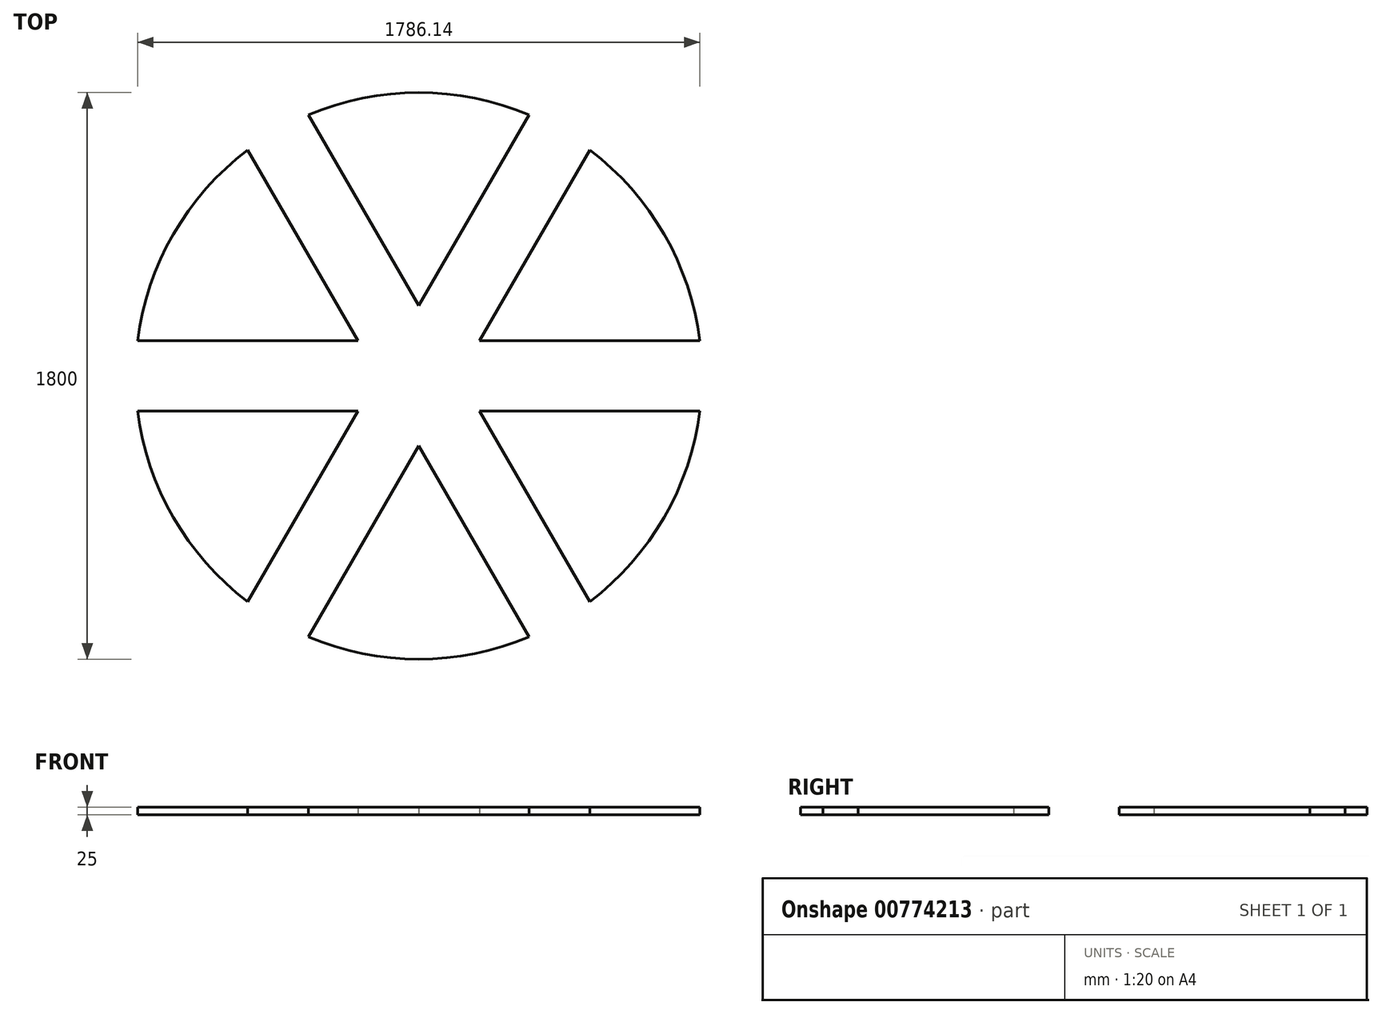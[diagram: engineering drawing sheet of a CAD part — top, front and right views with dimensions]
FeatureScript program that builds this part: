
annotation { "Feature Type Name" : "Feature", "Feature Type Description" : "" }
export const myFeature = defineFeature(function(context is Context, id is Id, definition is map)
    precondition{}
    {
        {
            var Q0;
            Q0=qCreatedBy(makeId("Top.planeOp"),FACE);
            var sketch = newSketch(context, id + "F0", { "sketchPlane" : qUnion([Q0])});
            skCircle(sketch, "E0", {"center": v(0, 0) * mm, "radius": 700 * mm});
            skCircle(sketch, "E1", {"center": v(0, 0) * mm, "radius": 900 * mm});
            skLineSegment(sketch, "E2", {"start": v(-350, 606.22) * mm, "end": v(-350, 829.16) * mm, "construction": true});
            skLineSegment(sketch, "E3", {"start": v(350, 606.22) * mm, "end": v(350, 829.16) * mm, "construction": true});
            skLineSegment(sketch, "E4", {"start": v(-350, 829.16) * mm, "end": v(0, 222.94) * mm});
            skLineSegment(sketch, "E5", {"start": v(0, 222.94) * mm, "end": v(375.18, 872.78) * mm});
            skArc(sketch, "E6", {"start": v(-375.18, 872.78) * mm, "mid": v(-475, -822.72) * mm, "end": v(943.44, 111.47) * mm});
            skLineSegment(sketch, "E7", {"start": v(-350, 829.16) * mm, "end": v(-375.18, 872.78) * mm});
            skLineSegment(sketch, "E8.1.0", {"start": v(-943.44, 111.47) * mm, "end": v(-193.07, 111.47) * mm});
            skLineSegment(sketch, "E8.1.1", {"start": v(-193.07, 111.47) * mm, "end": v(-568.25, 761.3) * mm});
            skLineSegment(sketch, "E8.2.0", {"start": v(-568.25, -761.3) * mm, "end": v(-193.07, -111.47) * mm});
            skLineSegment(sketch, "E8.2.1", {"start": v(-193.07, -111.47) * mm, "end": v(-943.44, -111.47) * mm});
            skLineSegment(sketch, "E8.3.0", {"start": v(375.18, -872.78) * mm, "end": v(0, -222.94) * mm});
            skLineSegment(sketch, "E8.3.1", {"start": v(0, -222.94) * mm, "end": v(-375.18, -872.78) * mm});
            skLineSegment(sketch, "E8.4.0", {"start": v(943.44, -111.47) * mm, "end": v(193.07, -111.47) * mm});
            skLineSegment(sketch, "E8.4.1", {"start": v(193.07, -111.47) * mm, "end": v(568.25, -761.3) * mm});
            skLineSegment(sketch, "E8.5.0", {"start": v(568.25, 761.3) * mm, "end": v(193.07, 111.47) * mm});
            skLineSegment(sketch, "E8.5.1", {"start": v(193.07, 111.47) * mm, "end": v(943.44, 111.47) * mm});
            skPoint(sketch, "E9.orphan", {"position": v(-893.07, 111.47) * mm});
            skPoint(sketch, "E10.orphan", {"position": v(-543.07, -717.69) * mm});
            skPoint(sketch, "E11.orphan", {"position": v(350, -829.16) * mm});
            skPoint(sketch, "E12.orphan", {"position": v(893.07, -111.47) * mm});
            skPoint(sketch, "E13.orphan", {"position": v(543.07, 717.69) * mm});
            skCircle(sketch, "E14", {"center": v(0, 0) * mm, "radius": 222.94 * mm, "construction": true});
            skLineSegment(sketch, "E15", {"start": v(-193.07, 111.47) * mm, "end": v(0, 222.94) * mm, "construction": true});
            skLineSegment(sketch, "E16", {"start": v(-568.25, 761.3) * mm, "end": v(-375.18, 872.78) * mm, "construction": true});
            skLineSegment(sketch, "E17", {"start": v(-96.54, 167.2) * mm, "end": v(-475, 822.72) * mm, "construction": true});
            skLineSegment(sketch, "E18", {"start": v(-111.47, 193.07) * mm, "end": v(-208, 137.34) * mm, "construction": true});
            skPoint(sketch, "E19.5.0.start.orphan", {"position": v(111.47, 193.07) * mm});
            skArc(sketch, "E20.trimOffspring", {"start": v(568.25, 761.3) * mm, "mid": v(475, 822.72) * mm, "end": v(375.18, 872.78) * mm});
            skSolve(sketch);
        }
        {
            var Q0;
            {var subQ0=sQuery(id+"F0.wireOp",EDGE,"E8.1.1");var subQ1=sQuery(id+"F0.wireOp",EDGE,"E0");var subQ2=makeQuery(id+"F0.imprint","INTERSECT",VERTEX,{"derivedFrom":[subQ1,subQ0]});Q0=makeQuery(id+"F0.imprint","IMPRINT",FACE,{"disambiguationData":[TD([[makeQuery(id+"F0.imprint","IMPRINT",EDGE,{"disambiguationData":[TD([[subQ2,-1.0]])],"derivedFrom":subQ1}),1.0]])]});}
            var Q1;
            {var subQ0=sQuery(id+"F0.wireOp",EDGE,"E8.1.1");var subQ1=sQuery(id+"F0.wireOp",EDGE,"E0");var subQ2=makeQuery(id+"F0.imprint","INTERSECT",VERTEX,{"derivedFrom":[subQ1,subQ0]});Q1=makeQuery(id+"F0.imprint","IMPRINT",FACE,{"disambiguationData":[TD([[makeQuery(id+"F0.imprint","IMPRINT",EDGE,{"disambiguationData":[TD([[subQ2,-1.0]])],"derivedFrom":subQ1}),-1.0]])]});}
            var Q2;
            {var subQ0=sQuery(id+"F0.wireOp",EDGE,"E5");var subQ1=sQuery(id+"F0.wireOp",EDGE,"E0");var subQ2=makeQuery(id+"F0.imprint","INTERSECT",VERTEX,{"derivedFrom":[subQ1,subQ0]});Q2=makeQuery(id+"F0.imprint","IMPRINT",FACE,{"disambiguationData":[TD([[makeQuery(id+"F0.imprint","IMPRINT",EDGE,{"disambiguationData":[TD([[subQ2,-1.0]])],"derivedFrom":subQ1}),1.0]])]});}
            var Q3;
            {var subQ0=sQuery(id+"F0.wireOp",EDGE,"E5");var subQ1=sQuery(id+"F0.wireOp",EDGE,"E0");var subQ2=makeQuery(id+"F0.imprint","INTERSECT",VERTEX,{"derivedFrom":[subQ1,subQ0]});Q3=makeQuery(id+"F0.imprint","IMPRINT",FACE,{"disambiguationData":[TD([[makeQuery(id+"F0.imprint","IMPRINT",EDGE,{"disambiguationData":[TD([[subQ2,-1.0]])],"derivedFrom":subQ1}),-1.0]])]});}
            var Q4;
            {var subQ0=sQuery(id+"F0.wireOp",EDGE,"E8.5.0");var subQ1=sQuery(id+"F0.wireOp",EDGE,"E0");var subQ2=makeQuery(id+"F0.imprint","INTERSECT",VERTEX,{"derivedFrom":[subQ1,subQ0]});Q4=makeQuery(id+"F0.imprint","IMPRINT",FACE,{"disambiguationData":[TD([[makeQuery(id+"F0.imprint","IMPRINT",EDGE,{"disambiguationData":[TD([[subQ2,1.0]])],"derivedFrom":subQ1}),1.0]])]});}
            var Q5;
            {var subQ0=sQuery(id+"F0.wireOp",EDGE,"E8.5.0");var subQ1=sQuery(id+"F0.wireOp",EDGE,"E0");var subQ2=makeQuery(id+"F0.imprint","INTERSECT",VERTEX,{"derivedFrom":[subQ1,subQ0]});Q5=makeQuery(id+"F0.imprint","IMPRINT",FACE,{"disambiguationData":[TD([[makeQuery(id+"F0.imprint","IMPRINT",EDGE,{"disambiguationData":[TD([[subQ2,1.0]])],"derivedFrom":subQ1}),-1.0]])]});}
            var Q6;
            {var subQ0=sQuery(id+"F0.wireOp",EDGE,"E8.4.1");var subQ1=sQuery(id+"F0.wireOp",EDGE,"E0");var subQ2=makeQuery(id+"F0.imprint","INTERSECT",VERTEX,{"derivedFrom":[subQ1,subQ0]});Q6=makeQuery(id+"F0.imprint","IMPRINT",FACE,{"disambiguationData":[TD([[makeQuery(id+"F0.imprint","IMPRINT",EDGE,{"disambiguationData":[TD([[subQ2,-1.0]])],"derivedFrom":subQ1}),1.0]])]});}
            var Q7;
            {var subQ0=sQuery(id+"F0.wireOp",EDGE,"E8.4.1");var subQ1=sQuery(id+"F0.wireOp",EDGE,"E0");var subQ2=makeQuery(id+"F0.imprint","INTERSECT",VERTEX,{"derivedFrom":[subQ1,subQ0]});Q7=makeQuery(id+"F0.imprint","IMPRINT",FACE,{"disambiguationData":[TD([[makeQuery(id+"F0.imprint","IMPRINT",EDGE,{"disambiguationData":[TD([[subQ2,-1.0]])],"derivedFrom":subQ1}),-1.0]])]});}
            var Q8;
            {var subQ0=sQuery(id+"F0.wireOp",EDGE,"E8.3.1");var subQ1=sQuery(id+"F0.wireOp",EDGE,"E0");var subQ2=makeQuery(id+"F0.imprint","INTERSECT",VERTEX,{"derivedFrom":[subQ1,subQ0]});Q8=makeQuery(id+"F0.imprint","IMPRINT",FACE,{"disambiguationData":[TD([[makeQuery(id+"F0.imprint","IMPRINT",EDGE,{"disambiguationData":[TD([[subQ2,-1.0]])],"derivedFrom":subQ1}),1.0]])]});}
            var Q9;
            {var subQ0=sQuery(id+"F0.wireOp",EDGE,"E8.3.1");var subQ1=sQuery(id+"F0.wireOp",EDGE,"E0");var subQ2=makeQuery(id+"F0.imprint","INTERSECT",VERTEX,{"derivedFrom":[subQ1,subQ0]});Q9=makeQuery(id+"F0.imprint","IMPRINT",FACE,{"disambiguationData":[TD([[makeQuery(id+"F0.imprint","IMPRINT",EDGE,{"disambiguationData":[TD([[subQ2,-1.0]])],"derivedFrom":subQ1}),-1.0]])]});}
            var Q10;
            {var subQ0=sQuery(id+"F0.wireOp",EDGE,"E8.2.1");var subQ1=sQuery(id+"F0.wireOp",EDGE,"E0");var subQ2=makeQuery(id+"F0.imprint","INTERSECT",VERTEX,{"derivedFrom":[subQ1,subQ0]});Q10=makeQuery(id+"F0.imprint","IMPRINT",FACE,{"disambiguationData":[TD([[makeQuery(id+"F0.imprint","IMPRINT",EDGE,{"disambiguationData":[TD([[subQ2,-1.0]])],"derivedFrom":subQ1}),-1.0]])]});}
            var Q11;
            {var subQ0=sQuery(id+"F0.wireOp",EDGE,"E8.2.1");var subQ1=sQuery(id+"F0.wireOp",EDGE,"E0");var subQ2=makeQuery(id+"F0.imprint","INTERSECT",VERTEX,{"derivedFrom":[subQ1,subQ0]});Q11=makeQuery(id+"F0.imprint","IMPRINT",FACE,{"disambiguationData":[TD([[makeQuery(id+"F0.imprint","IMPRINT",EDGE,{"disambiguationData":[TD([[subQ2,-1.0]])],"derivedFrom":subQ1}),1.0]])]});}
            extrude(context, id + "F1", {"entities" : qUnion([Q0, Q1, Q2, Q3, Q4, Q5, Q6, Q7, Q8, Q9, Q10, Q11]), "depth" : 25 * mm, "offsetDistance" : 25 * mm});
        }
    });
